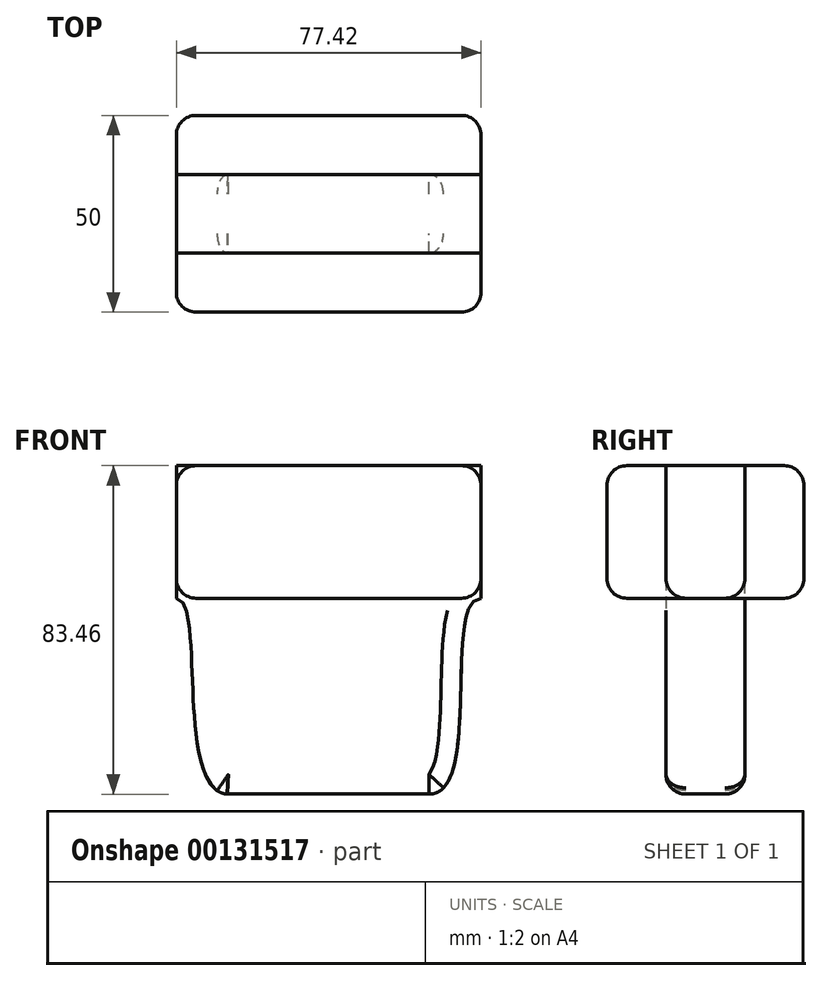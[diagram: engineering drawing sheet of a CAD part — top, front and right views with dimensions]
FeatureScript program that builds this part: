
annotation { "Feature Type Name" : "Feature", "Feature Type Description" : "" }
export const myFeature = defineFeature(function(context is Context, id is Id, definition is map)
    precondition{}
    {
        {
            var Q0;
            Q0=qCreatedBy(makeId("Front.planeOp"),FACE);
            var sketch = newSketch(context, id + "F0", { "sketchPlane" : qUnion([Q0])});
            skLineSegment(sketch, "E0.bottom", {"start": v(38.7, 33.6) * mm, "end": v(-38.7, 33.6) * mm});
            skLineSegment(sketch, "E0.top", {"start": v(38.7, -0.07) * mm, "end": v(-38.7, -0.07) * mm});
            skLineSegment(sketch, "E0.left", {"start": v(38.7, 33.6) * mm, "end": v(38.7, -0.07) * mm});
            skLineSegment(sketch, "E0.right", {"start": v(-38.7, 33.6) * mm, "end": v(-38.7, -0.07) * mm});
            skPoint(sketch, "E0.middle", {"position": v(0, 16.77) * mm});
            skLineSegment(sketch, "E1.bottom", {"start": v(25.53, -0.07) * mm, "end": v(-25.53, -0.07) * mm});
            skLineSegment(sketch, "E1.top", {"start": v(25.53, -49.85) * mm, "end": v(-25.53, -49.85) * mm});
            skPoint(sketch, "E1.middle", {"position": v(0, -24.96) * mm});
            skFitSpline(sketch, "E2", {"points": [v(-25.53, -49.85) * mm, v(-38.7, -0.07) * mm], "startDerivative": vector(-41.53, 0.73) * mm, "endDerivative": vector(-22.9, 0) * mm});
            skFitSpline(sketch, "E3", {"points": [v(25.53, -49.85) * mm, v(38.7, -0.07) * mm], "startDerivative": vector(41, 0) * mm, "endDerivative": vector(30.01, 0) * mm});
            skSolve(sketch);
        }
        {
            var Q0;
            Q0=makeQuery(id+"F0.imprint","IMPRINT",FACE,{"disambiguationData":[TD([[makeQuery(id+"F0.imprint","IMPRINT",EDGE,{"derivedFrom":sQuery(id+"F0.wireOp",EDGE,"E0.bottom")}),1.0]])]});
            extrude(context, id + "F1", {"entities" : qUnion([Q0]), "endBound" : BoundingType.SYMMETRIC, "depth" : 50 * mm});
        }
        {
            var Q0;
            Q0 = qSketchRegion(id + "F0", true);
            var Q1;
            {var subQ0=sQuery(id+"F0.wireOp",EDGE,"E1.bottom");Q1=makeQuery(id+"F0.imprint","IMPRINT",FACE,{"disambiguationData":[TD([[makeQuery(id+"F0.imprint","IMPRINT",EDGE,{"derivedFrom":subQ0}),1.0]])]});}
            extrude(context, id + "F2", {"entities" : qUnion([Q0, Q1]), "endBound" : BoundingType.SYMMETRIC, "depth" : 20 * mm});
        }
        {
            var Q0;
            Q0=makeQuery(id+"F1.opExtrude","CAP_EDGE",EDGE,{"disambiguationData":[OSD([sQuery(id+"F0.wireOp",EDGE,"E0.left")])],"isStart":false});
            var Q1;
            Q1=makeQuery(id+"F1.opExtrude","SWEPT_EDGE",EDGE,{"disambiguationData":[OSD([sQuery(id+"F0.wireOp",EDGE,"E0.top"),sQuery(id+"F0.wireOp",EDGE,"E0.left"),sQuery(id+"F0.wireOp",EDGE,"E3")])]});
            var Q2;
            Q2=makeQuery(id+"F1.opExtrude","CAP_EDGE",EDGE,{"disambiguationData":[OSD([sQuery(id+"F0.wireOp",EDGE,"E0.bottom")])],"isStart":false});
            var Q3;
            Q3=makeQuery(id+"F1.opExtrude","CAP_EDGE",EDGE,{"disambiguationData":[OSD([sQuery(id+"F0.wireOp",EDGE,"E0.top"),sQuery(id+"F0.wireOp",EDGE,"E1.bottom")])],"isStart":false});
            var Q4;
            Q4=makeQuery(id+"F1.opExtrude","CAP_EDGE",EDGE,{"disambiguationData":[OSD([sQuery(id+"F0.wireOp",EDGE,"E0.left")])],"isStart":true});
            var Q5;
            Q5=makeQuery(id+"F1.opExtrude","CAP_EDGE",EDGE,{"disambiguationData":[OSD([sQuery(id+"F0.wireOp",EDGE,"E0.bottom")])],"isStart":true});
            var Q6;
            Q6=makeQuery(id+"F1.opExtrude","CAP_EDGE",EDGE,{"disambiguationData":[OSD([sQuery(id+"F0.wireOp",EDGE,"E0.top"),sQuery(id+"F0.wireOp",EDGE,"E1.bottom")])],"isStart":true});
            var Q7;
            Q7=makeQuery(id+"F1.opExtrude","CAP_EDGE",EDGE,{"disambiguationData":[OSD([sQuery(id+"F0.wireOp",EDGE,"E0.right")])],"isStart":true});
            var Q8;
            Q8=makeQuery(id+"F1.opExtrude","SWEPT_EDGE",EDGE,{"disambiguationData":[OSD([sQuery(id+"F0.wireOp",EDGE,"E0.top"),sQuery(id+"F0.wireOp",EDGE,"E0.right"),sQuery(id+"F0.wireOp",EDGE,"E2")])]});
            var Q9;
            Q9=makeQuery(id+"F1.opExtrude","CAP_EDGE",EDGE,{"disambiguationData":[OSD([sQuery(id+"F0.wireOp",EDGE,"E0.right")])],"isStart":false});
            var Q10;
            Q10=makeQuery(id+"F2.opExtrude","CAP_EDGE",EDGE,{"disambiguationData":[OSD([sQuery(id+"F0.wireOp",EDGE,"E3")])],"isStart":false});
            var Q11;
            Q11=makeQuery(id+"F2.opExtrude","CAP_EDGE",EDGE,{"disambiguationData":[OSD([sQuery(id+"F0.wireOp",EDGE,"E3")])],"isStart":true});
            var Q12;
            Q12=makeQuery(id+"F2.opExtrude","CAP_EDGE",EDGE,{"disambiguationData":[OSD([sQuery(id+"F0.wireOp",EDGE,"E2")])],"isStart":false});
            var Q13;
            Q13=makeQuery(id+"F1.opExtrude","SWEPT_EDGE",EDGE,{"disambiguationData":[OSD([sQuery(id+"F0.wireOp",EDGE,"E0.bottom"),sQuery(id+"F0.wireOp",EDGE,"E0.left")])]});
            var Q14;
            Q14=makeQuery(id+"F1.opExtrude","SWEPT_EDGE",EDGE,{"disambiguationData":[OSD([sQuery(id+"F0.wireOp",EDGE,"E0.bottom"),sQuery(id+"F0.wireOp",EDGE,"E0.right")])]});
            fillet(context, id + "F3", {"entities" : qUnion([Q0, Q1, Q2, Q3, Q4, Q5, Q6, Q7, Q8, Q9, Q10, Q11, Q12, Q13, Q14]), "radius" : 5 * mm, "tangentPropagation" : true, "allowEdgeOverflow" : false});
        }
        {
            var Q0;
            Q0=makeQuery(id+"F2.opExtrude","CAP_EDGE",EDGE,{"disambiguationData":[OSD([sQuery(id+"F0.wireOp",EDGE,"E2")])],"isStart":true});
            fillet(context, id + "F4", {"entities" : qUnion([Q0]), "radius" : 5 * mm, "tangentPropagation" : true, "allowEdgeOverflow" : false});
        }
    });
